# Revit family: Faucet-Two_Handle-American_Standard-Colony_Soft-2475500_Series
name_source: partatom
category: Plumbing Fixtures
revit_build: Autodesk Revit 2018 (Build: 20170223_1515(x64)
units: mm (PartAtom-declared; Revit-internal decimal feet)

## family parameters
Always vertical = No
Cut with Voids When Loaded = No
OmniClass Number = 23.45.55.17
OmniClass Title = Mixing Faucets
Part Type = Normal
Room Calculation Point = No
Round Connector Dimension = Use Diameter
Shared = Yes
Work Plane-Based = No

## types (2) — shared parameters
ADA Compliant = Yes
Assembly Code = D2020300
CW Connection = Yes
CWFU = 1.5
Cold Water Connection Diameter = 1/2"
Default Elevation = 0"
Description = American Standard Colony Soft Two-Handle Centerset Bar Sink Faucet with Brass Gooseneck Spout.
Flow Rate = 2.2 Gpm (8.3Lpm)
HW Connection = Yes
HWFU = 1.5
Height = 13 1/16"
Hot Water Connection Diameter = 1/2"
Installation Type = Deck Mounted
Length = 9 3/4"
Manufacturer = American Standard
Product Documentation Link = https://americanstandard.box.com
Product Page URL = https://www.americanstandard-us.com
Revised Date = 08/14/2022
URL = http://www.americanstandard.ca
Vent Connection = No
WFU = 2
Waste Connection = No
Width = 5"

## per-type parameters (varying)
| type | Finish | Material |
| 2475500.075 | Brass-American Standard-075-Stainless Steel | Brass-American Standard-075-Stainless Steel |
| 2475500.002 | Brass-American Standard-002-Polished Chrome | Brass-American Standard-002-Polished Chrome |

note: column(s) folded — value = type name in every type: Model

## geometry (parser evidence)
native form markers: Sweep x2
no freeform markers — native parametric forms only
